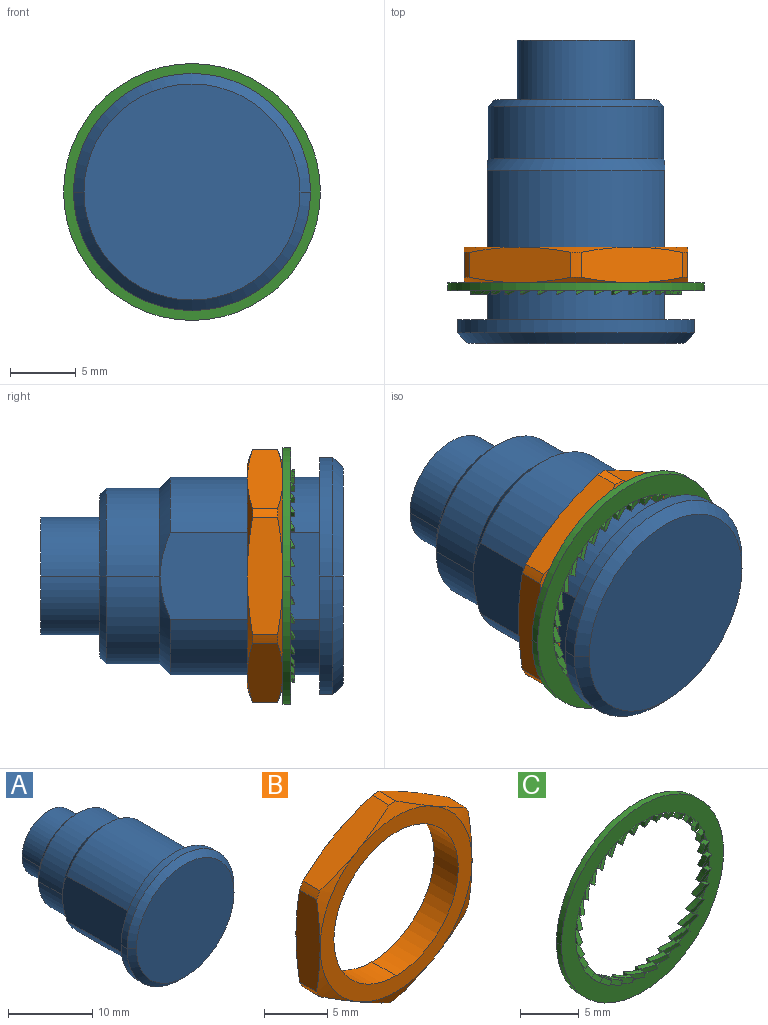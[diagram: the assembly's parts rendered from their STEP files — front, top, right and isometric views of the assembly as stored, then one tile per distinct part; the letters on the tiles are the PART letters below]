
ASSEMBLY  parts=3 mates=4
PART A: 20 faces, bbox 18x23x18 mm
  f0: cylinder r=4.45mm len=8.9mm, axis (0,-1,0), area 62.9mm2, adj f1,f2,f5
  f1: plane 8.9x8.9mm, normal (0,1,0), area 62.2mm2, adj f0,f2
  f2: cylinder r=4.45mm len=8.9mm, axis (0,-1,0), area 62.9mm2, adj f0,f1,f5
  f3: cylinder r=6.65mm len=13.3mm, axis (0,-1,0), area 83.6mm2, adj f4,f7,f18
  f4: cone r=6.15mm half-angle=45deg, axis (0,-1,0), area 14.2mm2, adj f3,f5,f6
  f5: plane 12.3x12.3mm, normal (0,1,0), area 56.6mm2, adj f0,f2,f4,f6
  f6: cone r=6.15mm half-angle=45deg, axis (0,-1,0), area 14.2mm2, adj f4,f5,f7
  f7: cylinder r=6.65mm len=13.3mm, axis (0,-1,0), area 83.6mm2, adj f3,f6,f17
  f8: plane 12.1x6.54mm, normal (1,0,0), area 77.4mm2, adj f9,f15,f16,f17,f18
  f9: cylinder r=7.5mm len=13.5mm, axis (0,-1,0), area 190.6mm2, adj f8,f15,f18,f19
  f10: plane 16.4x16.4mm, normal (0,-1,0), area 211.2mm2, adj f11,f12
  f11: cone r=8.2mm half-angle=45deg, axis (0,1,0), area 30.6mm2, adj f10,f12,f14
  f12: cone r=8.2mm half-angle=45deg, axis (0,1,0), area 30.6mm2, adj f10,f11,f13
  f13: cylinder r=9mm len=18mm, axis (0,-1,0), area 28.3mm2, adj f12,f14,f15
  f14: cylinder r=9mm len=18mm, axis (0,-1,0), area 28.3mm2, adj f11,f13,f15
  f15: plane 18x18mm, normal (0,1,0), area 84.4mm2, adj f8,f9,f13,f14,f16,f19
  f16: cylinder r=7.5mm len=13.5mm, axis (0,-1,0), area 190.6mm2, adj f8,f15,f17,f19
  f17: cone r=6.65mm half-angle=45deg, axis (0,-1,0), area 22mm2, adj f7,f8,f16,f18,f19
  f18: cone r=6.65mm half-angle=45deg, axis (0,-1,0), area 22mm2, adj f3,f8,f9,f17,f19
  f19: plane 12.1x6.54mm, normal (-1,0,0), area 77.4mm2, adj f9,f15,f16,f17,f18
PART B: 28 faces, bbox 19.2x2.7x19.2 mm
  f0: cone r=8.5mm half-angle=70deg, axis (0,1,0), area 4mm2, adj f1,f15,f17,f26
  f1: cylinder r=9.6mm len=1.9mm, axis (0,1,0), area 1.5mm2, adj f0,f15,f16,f17
  f2: cone r=8.5mm half-angle=70deg, axis (0,1,0), area 4mm2, adj f3,f13,f15,f26
  f3: cylinder r=9.6mm len=1.9mm, axis (0,1,0), area 1.5mm2, adj f2,f13,f14,f15
  f4: cylinder r=6.96mm len=13.92mm, axis (0,1,0), area 59mm2, adj f5,f26,f27
  f5: plane 17x17mm, normal (0,1,0), area 74.9mm2, adj f4,f8,f12,f14,f16,f20,f23,f27
  f6: cone r=8.5mm half-angle=70deg, axis (0,1,0), area 4mm2, adj f7,f9,f24,f26
  f7: cylinder r=9.6mm len=1.9mm, axis (0,1,0), area 1.5mm2, adj f6,f8,f9,f24
  f8: cone r=8.5mm half-angle=70deg, axis (0,-1,0), area 4mm2, adj f5,f7,f9,f24
  f9: plane 7.73x4.46mm, normal (0.5,0,-0.87), area 21.7mm2, adj f6,f7,f8,f10,f11,f12
  f10: cone r=8.5mm half-angle=70deg, axis (0,1,0), area 4mm2, adj f9,f11,f13,f26
  f11: cylinder r=9.6mm len=1.9mm, axis (0,1,0), area 1.5mm2, adj f9,f10,f12,f13
  f12: cone r=8.5mm half-angle=70deg, axis (0,-1,0), area 4mm2, adj f5,f9,f11,f13
  f13: plane 7.73x4.46mm, normal (-0.5,0,-0.87), area 21.7mm2, adj f2,f3,f10,f11,f12,f14
  f14: cone r=8.5mm half-angle=70deg, axis (0,-1,0), area 4mm2, adj f3,f5,f13,f15
  f15: plane 8.92x2.7mm, normal (-1,0,0), area 21.7mm2, adj f0,f1,f2,f3,f14,f16
  f16: cone r=8.5mm half-angle=70deg, axis (0,-1,0), area 4mm2, adj f1,f5,f15,f17
  f17: plane 7.73x4.46mm, normal (-0.5,0,0.87), area 21.7mm2, adj f0,f1,f16,f18,f19,f20
  f18: cone r=8.5mm half-angle=70deg, axis (0,1,0), area 4mm2, adj f17,f19,f21,f26
  f19: cylinder r=9.6mm len=1.9mm, axis (0,1,0), area 1.5mm2, adj f17,f18,f20,f21
  f20: cone r=8.5mm half-angle=70deg, axis (0,-1,0), area 4mm2, adj f5,f17,f19,f21
  f21: plane 7.73x4.46mm, normal (0.5,0,0.87), area 21.7mm2, adj f18,f19,f20,f22,f23,f25
  f22: cylinder r=9.6mm len=1.9mm, axis (0,1,0), area 1.5mm2, adj f21,f23,f24,f25
  f23: cone r=8.5mm half-angle=70deg, axis (0,-1,0), area 4mm2, adj f5,f21,f22,f24
  f24: plane 8.92x2.7mm, normal (1,0,0), area 21.7mm2, adj f6,f7,f8,f22,f23,f25
  f25: cone r=8.5mm half-angle=70deg, axis (0,1,0), area 4mm2, adj f21,f22,f24,f26
  f26: plane 17x17mm, normal (0,-1,0), area 74.9mm2, adj f0,f2,f4,f6,f10,f18,f25,f27
  f27: cylinder r=6.96mm len=13.92mm, axis (0,1,0), area 59mm2, adj f4,f5,f26
PART C: 276 faces, bbox 19.5x1.2x19.5 mm
  f0: cylinder r=8.05mm len=0.68mm, axis (0,1,0), area 0.1mm2, adj f269,f271,f272
  f1: cylinder r=8.05mm len=0.68mm, axis (0,1,0), area 0.1mm2, adj f266,f273,f274
  f2: bspline ~1.51x0.79mm, area 0.8mm2, adj f3,f4,f8,f9,f13
  f3: cylinder r=8.05mm len=0.67mm, axis (0,1,0), area 0.1mm2, adj f2,f4,f269
  f4: plane 0.55x0.5mm, normal (-0.1,0,-0.99), area 0.3mm2, adj f2,f3,f5,f7,f8
  f5: cylinder r=8.05mm len=1.6mm, axis (0,-1,0), area 0.3mm2, adj f4,f7,f266,f269,f272,f273
  f6: cylinder r=8.05mm len=0.66mm, axis (0,1,0), area 0.1mm2, adj f7,f9,f266
  f7: bspline ~1.51x0.79mm, area 0.8mm2, adj f4,f5,f6,f8,f9
  f8: cylinder r=7.55mm len=1.37mm, axis (0,1,0), area 0.8mm2, adj f2,f4,f7,f9
  f9: plane 0.55x0.48mm, normal (0.26,0,0.97), area 0.3mm2, adj f2,f6,f7,f8,f13
  f10: bspline ~1.53x1.02mm, area 0.8mm2, adj f11,f12,f16,f17,f21
  f11: cylinder r=8.05mm len=0.64mm, axis (0,1,0), area 0.1mm2, adj f10,f12,f269
  f12: plane 0.55x0.48mm, normal (-0.29,0,-0.96), area 0.3mm2, adj f10,f11,f13,f15,f16
  f13: cylinder r=8.05mm len=1.54mm, axis (0,-1,0), area 0.3mm2, adj f2,f9,f12,f15,f266,f269
  f14: cylinder r=8.05mm len=0.62mm, axis (0,1,0), area 0.1mm2, adj f15,f17,f266
  f15: bspline ~1.53x1.02mm, area 0.8mm2, adj f12,f13,f14,f16,f17
  f16: cylinder r=7.55mm len=1.3mm, axis (0,1,0), area 0.8mm2, adj f10,f12,f15,f17
  f17: plane 0.55x0.45mm, normal (0.43,0,0.9), area 0.3mm2, adj f10,f14,f15,f16,f21
  f18: bspline ~1.5x1.21mm, area 0.8mm2, adj f19,f20,f24,f25,f29
  f19: cylinder r=8.05mm len=0.59mm, axis (0,1,0), area 0.1mm2, adj f18,f20,f269
  f20: plane 0.55x0.44mm, normal (-0.46,0,-0.89), area 0.3mm2, adj f18,f19,f21,f23,f24
  f21: cylinder r=8.05mm len=1.44mm, axis (0,-1,0), area 0.3mm2, adj f10,f17,f20,f23,f266,f269
  f22: cylinder r=8.05mm len=0.56mm, axis (0,1,0), area 0.1mm2, adj f23,f25,f266
  f23: bspline ~1.5x1.21mm, area 0.8mm2, adj f20,f21,f22,f24,f25
  f24: cylinder r=7.55mm len=1.2mm, axis (0,1,0), area 0.8mm2, adj f18,f20,f23,f25
  f25: plane 0.55x0.4mm, normal (0.59,0,0.81), area 0.3mm2, adj f18,f22,f23,f24,f29
  f26: bspline ~1.42x1.36mm, area 0.8mm2, adj f27,f28,f32,f33,f37
  f27: cylinder r=8.05mm len=0.52mm, axis (0,1,0), area 0.1mm2, adj f26,f28,f269
  f28: plane 0.55x0.4mm, normal (-0.61,0,-0.79), area 0.3mm2, adj f26,f27,f29,f31,f32
  f29: cylinder r=8.05mm len=1.28mm, axis (0,-1,0), area 0.3mm2, adj f18,f25,f28,f31,f266,f269
  f30: cylinder r=8.05mm len=0.48mm, axis (0,1,0), area 0.1mm2, adj f31,f33,f266
  f31: bspline ~1.42x1.36mm, area 0.8mm2, adj f28,f29,f30,f32,f33
  f32: cylinder r=7.55mm len=1.2mm, axis (0,1,0), area 0.8mm2, adj f26,f28,f31,f33
  f33: plane 0.55x0.37mm, normal (0.73,0,0.68), area 0.3mm2, adj f26,f30,f31,f32,f37
  f34: bspline ~1.47x1.29mm, area 0.8mm2, adj f35,f36,f40,f41,f45
  f35: cylinder r=8.05mm len=0.52mm, axis (0,1,0), area 0.1mm2, adj f34,f36,f269
  f36: plane 0.55x0.37mm, normal (-0.75,0,-0.66), area 0.3mm2, adj f34,f35,f37,f39,f40
  f37: cylinder r=8.05mm len=1.19mm, axis (0,-1,0), area 0.3mm2, adj f26,f33,f36,f39,f266,f269
  f38: cylinder r=8.05mm len=0.56mm, axis (0,1,0), area 0.1mm2, adj f39,f41,f266
  f39: bspline ~1.47x1.29mm, area 0.8mm2, adj f36,f37,f38,f40,f41
  f40: cylinder r=7.55mm len=1.2mm, axis (0,1,0), area 0.8mm2, adj f34,f36,f39,f41
  f41: plane 0.55x0.42mm, normal (0.84,0,0.54), area 0.3mm2, adj f34,f38,f39,f40,f45
  f42: bspline ~1.53x1.12mm, area 0.8mm2, adj f43,f44,f48,f49,f53
  f43: cylinder r=8.05mm len=0.59mm, axis (0,1,0), area 0.1mm2, adj f42,f44,f269
  f44: plane 0.55x0.43mm, normal (-0.86,0,-0.52), area 0.3mm2, adj f42,f43,f45,f47,f48
  f45: cylinder r=8.05mm len=1.36mm, axis (0,-1,0), area 0.3mm2, adj f34,f41,f44,f47,f266,f269
  f46: cylinder r=8.05mm len=0.62mm, axis (0,1,0), area 0.1mm2, adj f47,f49,f266
  f47: bspline ~1.53x1.12mm, area 0.8mm2, adj f44,f45,f46,f48,f49
  f48: cylinder r=7.55mm len=1.25mm, axis (0,1,0), area 0.8mm2, adj f42,f44,f47,f49
  f49: plane 0.55x0.46mm, normal (0.93,0,0.37), area 0.3mm2, adj f42,f46,f47,f48,f53
  f50: bspline ~1.53x0.91mm, area 0.8mm2, adj f51,f52,f56,f57,f61
  f51: cylinder r=8.05mm len=0.64mm, axis (0,1,0), area 0.1mm2, adj f50,f52,f269
  f52: plane 0.55x0.47mm, normal (-0.94,0,-0.35), area 0.3mm2, adj f50,f51,f53,f55,f56
  f53: cylinder r=8.05mm len=1.5mm, axis (0,-1,0), area 0.3mm2, adj f42,f49,f52,f55,f266,f269
  f54: cylinder r=8.05mm len=0.66mm, axis (0,1,0), area 0.1mm2, adj f55,f57,f266
  f55: bspline ~1.53x0.91mm, area 0.8mm2, adj f52,f53,f54,f56,f57
  f56: cylinder r=7.55mm len=1.34mm, axis (0,1,0), area 0.8mm2, adj f50,f52,f55,f57
  f57: plane 0.55x0.49mm, normal (0.98,0,0.2), area 0.3mm2, adj f50,f54,f55,f56,f61
  f58: bspline ~1.48x0.67mm, area 0.8mm2, adj f59,f60,f64,f65,f69
  f59: cylinder r=8.05mm len=0.67mm, axis (0,1,0), area 0.1mm2, adj f58,f60,f269
  f60: plane 0.55x0.49mm, normal (-0.99,0,-0.17), area 0.3mm2, adj f58,f59,f61,f63,f64
  f61: cylinder r=8.05mm len=1.58mm, axis (0,-1,0), area 0.3mm2, adj f50,f57,f60,f63,f266,f269
  f62: cylinder r=8.05mm len=0.68mm, axis (0,1,0), area 0.1mm2, adj f63,f65,f266
  f63: bspline ~1.48x0.67mm, area 0.8mm2, adj f60,f61,f62,f64,f65
  f64: cylinder r=7.55mm len=1.39mm, axis (0,1,0), area 0.8mm2, adj f58,f60,f63,f65
  f65: plane 0.55x0.5mm, normal (1,0,0.01), area 0.3mm2, adj f58,f62,f63,f64,f69
  f66: bspline ~1.48x0.67mm, area 0.8mm2, adj f67,f68,f72,f73,f77
  f67: cylinder r=8.05mm len=0.68mm, axis (0,1,0), area 0.1mm2, adj f66,f68,f269
  f68: plane 0.55x0.5mm, normal (-1,0,0.01), area 0.3mm2, adj f66,f67,f69,f71,f72
  f69: cylinder r=8.05mm len=1.6mm, axis (0,-1,0), area 0.3mm2, adj f58,f65,f68,f71,f266,f269
  f70: cylinder r=8.05mm len=0.67mm, axis (0,1,0), area 0.1mm2, adj f71,f73,f266
  f71: bspline ~1.48x0.67mm, area 0.8mm2, adj f68,f69,f70,f72,f73
  f72: cylinder r=7.55mm len=1.39mm, axis (0,1,0), area 0.8mm2, adj f66,f68,f71,f73
  f73: plane 0.55x0.49mm, normal (0.99,0,-0.17), area 0.3mm2, adj f66,f70,f71,f72,f77
  f74: bspline ~1.53x0.91mm, area 0.8mm2, adj f75,f76,f80,f81,f85
  f75: cylinder r=8.05mm len=0.66mm, axis (0,1,0), area 0.1mm2, adj f74,f76,f269
  f76: plane 0.55x0.49mm, normal (-0.98,0,0.2), area 0.3mm2, adj f74,f75,f77,f79,f80
  f77: cylinder r=8.05mm len=1.58mm, axis (0,-1,0), area 0.3mm2, adj f66,f73,f76,f79,f266,f269
  f78: cylinder r=8.05mm len=0.64mm, axis (0,1,0), area 0.1mm2, adj f79,f81,f266
  f79: bspline ~1.53x0.91mm, area 0.8mm2, adj f76,f77,f78,f80,f81
  f80: cylinder r=7.55mm len=1.34mm, axis (0,1,0), area 0.8mm2, adj f74,f76,f79,f81
  f81: plane 0.55x0.47mm, normal (0.94,0,-0.35), area 0.3mm2, adj f74,f78,f79,f80,f85
  f82: bspline ~1.53x1.12mm, area 0.8mm2, adj f83,f84,f88,f89,f93
  f83: cylinder r=8.05mm len=0.62mm, axis (0,1,0), area 0.1mm2, adj f82,f84,f269
  f84: plane 0.55x0.46mm, normal (-0.93,0,0.37), area 0.3mm2, adj f82,f83,f85,f87,f88
  f85: cylinder r=8.05mm len=1.5mm, axis (0,-1,0), area 0.3mm2, adj f74,f81,f84,f87,f266,f269
  f86: cylinder r=8.05mm len=0.59mm, axis (0,1,0), area 0.1mm2, adj f87,f89,f266
  f87: bspline ~1.53x1.12mm, area 0.8mm2, adj f84,f85,f86,f88,f89
  f88: cylinder r=7.55mm len=1.25mm, axis (0,1,0), area 0.8mm2, adj f82,f84,f87,f89
  f89: plane 0.55x0.43mm, normal (0.86,0,-0.52), area 0.3mm2, adj f82,f86,f87,f88,f93
  f90: bspline ~1.47x1.29mm, area 0.8mm2, adj f91,f92,f96,f97,f101
  f91: cylinder r=8.05mm len=0.56mm, axis (0,1,0), area 0.1mm2, adj f90,f92,f269
  f92: plane 0.55x0.42mm, normal (-0.84,0,0.54), area 0.3mm2, adj f90,f91,f93,f95,f96
  f93: cylinder r=8.05mm len=1.36mm, axis (0,-1,0), area 0.3mm2, adj f82,f89,f92,f95,f266,f269
  f94: cylinder r=8.05mm len=0.52mm, axis (0,1,0), area 0.1mm2, adj f95,f97,f266
  f95: bspline ~1.47x1.29mm, area 0.8mm2, adj f92,f93,f94,f96,f97
  f96: cylinder r=7.55mm len=1.2mm, axis (0,1,0), area 0.8mm2, adj f90,f92,f95,f97
  f97: plane 0.55x0.37mm, normal (0.75,0,-0.66), area 0.3mm2, adj f90,f94,f95,f96,f101
  f98: bspline ~1.42x1.36mm, area 0.8mm2, adj f99,f100,f104,f105,f109
  f99: cylinder r=8.05mm len=0.48mm, axis (0,1,0), area 0.1mm2, adj f98,f100,f269
  f100: plane 0.55x0.37mm, normal (-0.73,0,0.68), area 0.3mm2, adj f98,f99,f101,f103,f104
  f101: cylinder r=8.05mm len=1.19mm, axis (0,-1,0), area 0.3mm2, adj f90,f97,f100,f103,f266,f269
  f102: cylinder r=8.05mm len=0.52mm, axis (0,1,0), area 0.1mm2, adj f103,f105,f266
  f103: bspline ~1.42x1.36mm, area 0.8mm2, adj f100,f101,f102,f104,f105
  f104: cylinder r=7.55mm len=1.2mm, axis (0,1,0), area 0.8mm2, adj f98,f100,f103,f105
  f105: plane 0.55x0.4mm, normal (0.61,0,-0.79), area 0.3mm2, adj f98,f102,f103,f104,f109
  f106: bspline ~1.5x1.21mm, area 0.8mm2, adj f107,f108,f112,f113,f117
  f107: cylinder r=8.05mm len=0.56mm, axis (0,1,0), area 0.1mm2, adj f106,f108,f269
  f108: plane 0.55x0.4mm, normal (-0.59,0,0.81), area 0.3mm2, adj f106,f107,f109,f111,f112
  f109: cylinder r=8.05mm len=1.28mm, axis (0,-1,0), area 0.3mm2, adj f98,f105,f108,f111,f266,f269
  f110: cylinder r=8.05mm len=0.59mm, axis (0,1,0), area 0.1mm2, adj f111,f113,f266
  f111: bspline ~1.5x1.21mm, area 0.8mm2, adj f108,f109,f110,f112,f113
  f112: cylinder r=7.55mm len=1.2mm, axis (0,1,0), area 0.8mm2, adj f106,f108,f111,f113
  f113: plane 0.55x0.44mm, normal (0.46,0,-0.89), area 0.3mm2, adj f106,f110,f111,f112,f117
  f114: bspline ~1.53x1.02mm, area 0.8mm2, adj f115,f116,f120,f121,f125
  f115: cylinder r=8.05mm len=0.62mm, axis (0,1,0), area 0.1mm2, adj f114,f116,f269
  f116: plane 0.55x0.45mm, normal (-0.43,0,0.9), area 0.3mm2, adj f114,f115,f117,f119,f120
  f117: cylinder r=8.05mm len=1.44mm, axis (0,-1,0), area 0.3mm2, adj f106,f113,f116,f119,f266,f269
  f118: cylinder r=8.05mm len=0.64mm, axis (0,1,0), area 0.1mm2, adj f119,f121,f266
  f119: bspline ~1.53x1.02mm, area 0.8mm2, adj f116,f117,f118,f120,f121
  f120: cylinder r=7.55mm len=1.3mm, axis (0,1,0), area 0.8mm2, adj f114,f116,f119,f121
  f121: plane 0.55x0.48mm, normal (0.29,0,-0.96), area 0.3mm2, adj f114,f118,f119,f120,f125
  f122: bspline ~1.51x0.79mm, area 0.8mm2, adj f123,f124,f128,f129,f133
  f123: cylinder r=8.05mm len=0.66mm, axis (0,1,0), area 0.1mm2, adj f122,f124,f269
  f124: plane 0.55x0.48mm, normal (-0.26,0,0.97), area 0.3mm2, adj f122,f123,f125,f127,f128
  f125: cylinder r=8.05mm len=1.54mm, axis (0,-1,0), area 0.3mm2, adj f114,f121,f124,f127,f266,f269
  f126: cylinder r=8.05mm len=0.67mm, axis (0,1,0), area 0.1mm2, adj f127,f129,f266
  f127: bspline ~1.51x0.79mm, area 0.8mm2, adj f124,f125,f126,f128,f129
  f128: cylinder r=7.55mm len=1.37mm, axis (0,1,0), area 0.8mm2, adj f122,f124,f127,f129
  f129: plane 0.55x0.5mm, normal (0.1,0,-0.99), area 0.3mm2, adj f122,f126,f127,f128,f133
  f130: bspline ~1.48x0.65mm, area 0.8mm2, adj f131,f132,f136,f137,f141
  f131: cylinder r=8.05mm len=0.68mm, axis (0,1,0), area 0.1mm2, adj f130,f132,f269
  f132: plane 0.55x0.5mm, normal (-0.08,0,1), area 0.3mm2, adj f130,f131,f133,f135,f136
  f133: cylinder r=8.05mm len=1.6mm, axis (0,-1,0), area 0.3mm2, adj f122,f129,f132,f135,f266,f269
  f134: cylinder r=8.05mm len=0.68mm, axis (0,1,0), area 0.1mm2, adj f135,f137,f266
  f135: bspline ~1.48x0.65mm, area 0.8mm2, adj f132,f133,f134,f136,f137
  f136: cylinder r=7.55mm len=1.39mm, axis (0,1,0), area 0.8mm2, adj f130,f132,f135,f137
  f137: plane 0.55x0.5mm, normal (-0.08,0,-1), area 0.3mm2, adj f130,f134,f135,f136,f141
  f138: bspline ~1.51x0.79mm, area 0.8mm2, adj f139,f140,f144,f145,f149
  f139: cylinder r=8.05mm len=0.67mm, axis (0,1,0), area 0.1mm2, adj f138,f140,f269
  f140: plane 0.55x0.5mm, normal (0.1,0,0.99), area 0.3mm2, adj f138,f139,f141,f143,f144
  f141: cylinder r=8.05mm len=1.6mm, axis (0,-1,0), area 0.3mm2, adj f130,f137,f140,f143,f266,f269
  f142: cylinder r=8.05mm len=0.66mm, axis (0,1,0), area 0.1mm2, adj f143,f145,f266
  f143: bspline ~1.51x0.79mm, area 0.8mm2, adj f140,f141,f142,f144,f145
  f144: cylinder r=7.55mm len=1.37mm, axis (0,1,0), area 0.8mm2, adj f138,f140,f143,f145
  f145: plane 0.55x0.48mm, normal (-0.26,0,-0.97), area 0.3mm2, adj f138,f142,f143,f144,f149
  f146: bspline ~1.53x1.02mm, area 0.8mm2, adj f147,f148,f152,f153,f157
  f147: cylinder r=8.05mm len=0.64mm, axis (0,1,0), area 0.1mm2, adj f146,f148,f269
  f148: plane 0.55x0.48mm, normal (0.29,0,0.96), area 0.3mm2, adj f146,f147,f149,f151,f152
  f149: cylinder r=8.05mm len=1.54mm, axis (0,-1,0), area 0.3mm2, adj f138,f145,f148,f151,f266,f269
  f150: cylinder r=8.05mm len=0.62mm, axis (0,1,0), area 0.1mm2, adj f151,f153,f266
  f151: bspline ~1.53x1.02mm, area 0.8mm2, adj f148,f149,f150,f152,f153
  f152: cylinder r=7.55mm len=1.3mm, axis (0,1,0), area 0.8mm2, adj f146,f148,f151,f153
  f153: plane 0.55x0.45mm, normal (-0.43,0,-0.9), area 0.3mm2, adj f146,f150,f151,f152,f157
  f154: bspline ~1.5x1.21mm, area 0.8mm2, adj f155,f156,f160,f161,f165
  f155: cylinder r=8.05mm len=0.59mm, axis (0,1,0), area 0.1mm2, adj f154,f156,f269
  f156: plane 0.55x0.44mm, normal (0.46,0,0.89), area 0.3mm2, adj f154,f155,f157,f159,f160
  f157: cylinder r=8.05mm len=1.44mm, axis (0,-1,0), area 0.3mm2, adj f146,f153,f156,f159,f266,f269
  f158: cylinder r=8.05mm len=0.56mm, axis (0,1,0), area 0.1mm2, adj f159,f161,f266
  f159: bspline ~1.5x1.21mm, area 0.8mm2, adj f156,f157,f158,f160,f161
  f160: cylinder r=7.55mm len=1.2mm, axis (0,1,0), area 0.8mm2, adj f154,f156,f159,f161
  f161: plane 0.55x0.4mm, normal (-0.59,0,-0.81), area 0.3mm2, adj f154,f158,f159,f160,f165
  f162: bspline ~1.42x1.36mm, area 0.8mm2, adj f163,f164,f168,f169,f173
  f163: cylinder r=8.05mm len=0.52mm, axis (0,1,0), area 0.1mm2, adj f162,f164,f269
  f164: plane 0.55x0.4mm, normal (0.61,0,0.79), area 0.3mm2, adj f162,f163,f165,f167,f168
  f165: cylinder r=8.05mm len=1.28mm, axis (0,-1,0), area 0.3mm2, adj f154,f161,f164,f167,f266,f269
  f166: cylinder r=8.05mm len=0.48mm, axis (0,1,0), area 0.1mm2, adj f167,f169,f266
  f167: bspline ~1.42x1.36mm, area 0.8mm2, adj f164,f165,f166,f168,f169
  f168: cylinder r=7.55mm len=1.2mm, axis (0,1,0), area 0.8mm2, adj f162,f164,f167,f169
  f169: plane 0.55x0.37mm, normal (-0.73,0,-0.68), area 0.3mm2, adj f162,f166,f167,f168,f173
  f170: bspline ~1.47x1.29mm, area 0.8mm2, adj f171,f172,f176,f177,f181
  f171: cylinder r=8.05mm len=0.52mm, axis (0,1,0), area 0.1mm2, adj f170,f172,f269
  f172: plane 0.55x0.37mm, normal (0.75,0,0.66), area 0.3mm2, adj f170,f171,f173,f175,f176
  f173: cylinder r=8.05mm len=1.19mm, axis (0,-1,0), area 0.3mm2, adj f162,f169,f172,f175,f266,f269
  f174: cylinder r=8.05mm len=0.56mm, axis (0,1,0), area 0.1mm2, adj f175,f177,f266
  f175: bspline ~1.47x1.29mm, area 0.8mm2, adj f172,f173,f174,f176,f177
  f176: cylinder r=7.55mm len=1.2mm, axis (0,1,0), area 0.8mm2, adj f170,f172,f175,f177
  f177: plane 0.55x0.42mm, normal (-0.84,0,-0.54), area 0.3mm2, adj f170,f174,f175,f176,f181
  f178: bspline ~1.53x1.12mm, area 0.8mm2, adj f179,f180,f184,f185,f189
  f179: cylinder r=8.05mm len=0.59mm, axis (0,1,0), area 0.1mm2, adj f178,f180,f269
  f180: plane 0.55x0.43mm, normal (0.86,0,0.52), area 0.3mm2, adj f178,f179,f181,f183,f184
  f181: cylinder r=8.05mm len=1.36mm, axis (0,-1,0), area 0.3mm2, adj f170,f177,f180,f183,f266,f269
  f182: cylinder r=8.05mm len=0.62mm, axis (0,1,0), area 0.1mm2, adj f183,f185,f266
  f183: bspline ~1.53x1.12mm, area 0.8mm2, adj f180,f181,f182,f184,f185
  f184: cylinder r=7.55mm len=1.25mm, axis (0,1,0), area 0.8mm2, adj f178,f180,f183,f185
  f185: plane 0.55x0.46mm, normal (-0.93,0,-0.37), area 0.3mm2, adj f178,f182,f183,f184,f189
  f186: bspline ~1.53x0.91mm, area 0.8mm2, adj f187,f188,f192,f193,f197
  f187: cylinder r=8.05mm len=0.64mm, axis (0,1,0), area 0.1mm2, adj f186,f188,f269
  f188: plane 0.55x0.47mm, normal (0.94,0,0.35), area 0.3mm2, adj f186,f187,f189,f191,f192
  f189: cylinder r=8.05mm len=1.5mm, axis (0,-1,0), area 0.3mm2, adj f178,f185,f188,f191,f266,f269
  f190: cylinder r=8.05mm len=0.66mm, axis (0,1,0), area 0.1mm2, adj f191,f193,f266
  f191: bspline ~1.53x0.91mm, area 0.8mm2, adj f188,f189,f190,f192,f193
  f192: cylinder r=7.55mm len=1.34mm, axis (0,1,0), area 0.8mm2, adj f186,f188,f191,f193
  f193: plane 0.55x0.49mm, normal (-0.98,0,-0.2), area 0.3mm2, adj f186,f190,f191,f192,f197
  f194: bspline ~1.48x0.67mm, area 0.8mm2, adj f195,f196,f200,f201,f265
  f195: cylinder r=8.05mm len=0.67mm, axis (0,1,0), area 0.1mm2, adj f194,f196,f269
  f196: plane 0.55x0.49mm, normal (0.99,0,0.17), area 0.3mm2, adj f194,f195,f197,f199,f200
  f197: cylinder r=8.05mm len=1.58mm, axis (0,-1,0), area 0.3mm2, adj f186,f193,f196,f199,f266,f269
  f198: cylinder r=8.05mm len=0.68mm, axis (0,1,0), area 0.1mm2, adj f199,f201,f266
  f199: bspline ~1.48x0.67mm, area 0.8mm2, adj f196,f197,f198,f200,f201
  f200: cylinder r=7.55mm len=1.39mm, axis (0,1,0), area 0.8mm2, adj f194,f196,f199,f201
  f201: plane 0.55x0.5mm, normal (-1,0,-0.01), area 0.3mm2, adj f194,f198,f199,f200,f265
  f202: cylinder r=8.05mm len=0.67mm, axis (0,1,0), area 0.1mm2, adj f261,f262,f266
  f203: cylinder r=8.05mm len=0.64mm, axis (0,1,0), area 0.1mm2, adj f254,f255,f266
  f204: cylinder r=8.05mm len=0.59mm, axis (0,1,0), area 0.1mm2, adj f247,f248,f266
  f205: cylinder r=8.05mm len=0.52mm, axis (0,1,0), area 0.1mm2, adj f240,f241,f266
  f206: cylinder r=8.05mm len=0.52mm, axis (0,1,0), area 0.1mm2, adj f233,f234,f266
  f207: cylinder r=8.05mm len=0.59mm, axis (0,1,0), area 0.1mm2, adj f226,f227,f266
  f208: cylinder r=8.05mm len=0.64mm, axis (0,1,0), area 0.1mm2, adj f219,f220,f266
  f209: cylinder r=8.05mm len=0.67mm, axis (0,1,0), area 0.1mm2, adj f212,f213,f266
  f210: cylinder r=8.05mm len=0.66mm, axis (0,1,0), area 0.1mm2, adj f211,f215,f269
  f211: bspline ~1.51x0.79mm, area 0.8mm2, adj f210,f212,f214,f215,f270
  f212: plane 0.55x0.5mm, normal (-0.1,0,0.99), area 0.3mm2, adj f209,f211,f213,f214,f270
  f213: bspline ~1.51x0.79mm, area 0.8mm2, adj f209,f212,f214,f215,f216
  f214: cylinder r=7.55mm len=1.37mm, axis (0,1,0), area 0.8mm2, adj f211,f212,f213,f215
  f215: plane 0.55x0.48mm, normal (0.26,0,-0.97), area 0.3mm2, adj f210,f211,f213,f214,f216
  f216: cylinder r=8.05mm len=1.54mm, axis (0,-1,0), area 0.3mm2, adj f213,f215,f218,f219,f266,f269
  f217: cylinder r=8.05mm len=0.62mm, axis (0,1,0), area 0.1mm2, adj f218,f222,f269
  f218: bspline ~1.53x1.02mm, area 0.8mm2, adj f216,f217,f219,f221,f222
  f219: plane 0.55x0.48mm, normal (-0.29,0,0.96), area 0.3mm2, adj f208,f216,f218,f220,f221
  f220: bspline ~1.53x1.02mm, area 0.8mm2, adj f208,f219,f221,f222,f223
  f221: cylinder r=7.55mm len=1.3mm, axis (0,1,0), area 0.8mm2, adj f218,f219,f220,f222
  f222: plane 0.55x0.45mm, normal (0.43,0,-0.9), area 0.3mm2, adj f217,f218,f220,f221,f223
  f223: cylinder r=8.05mm len=1.44mm, axis (0,-1,0), area 0.3mm2, adj f220,f222,f225,f226,f266,f269
  f224: cylinder r=8.05mm len=0.56mm, axis (0,1,0), area 0.1mm2, adj f225,f229,f269
  f225: bspline ~1.5x1.21mm, area 0.8mm2, adj f223,f224,f226,f228,f229
  f226: plane 0.55x0.44mm, normal (-0.46,0,0.89), area 0.3mm2, adj f207,f223,f225,f227,f228
  f227: bspline ~1.5x1.21mm, area 0.8mm2, adj f207,f226,f228,f229,f230
  f228: cylinder r=7.55mm len=1.2mm, axis (0,1,0), area 0.8mm2, adj f225,f226,f227,f229
  f229: plane 0.55x0.4mm, normal (0.59,0,-0.81), area 0.3mm2, adj f224,f225,f227,f228,f230
  f230: cylinder r=8.05mm len=1.28mm, axis (0,-1,0), area 0.3mm2, adj f227,f229,f232,f233,f266,f269
  f231: cylinder r=8.05mm len=0.48mm, axis (0,1,0), area 0.1mm2, adj f232,f236,f269
  f232: bspline ~1.42x1.36mm, area 0.8mm2, adj f230,f231,f233,f235,f236
  f233: plane 0.55x0.4mm, normal (-0.61,0,0.79), area 0.3mm2, adj f206,f230,f232,f234,f235
  f234: bspline ~1.42x1.36mm, area 0.8mm2, adj f206,f233,f235,f236,f237
  f235: cylinder r=7.55mm len=1.2mm, axis (0,1,0), area 0.8mm2, adj f232,f233,f234,f236
  f236: plane 0.55x0.37mm, normal (0.73,0,-0.68), area 0.3mm2, adj f231,f232,f234,f235,f237
  f237: cylinder r=8.05mm len=1.19mm, axis (0,-1,0), area 0.3mm2, adj f234,f236,f239,f240,f266,f269
  f238: cylinder r=8.05mm len=0.56mm, axis (0,1,0), area 0.1mm2, adj f239,f243,f269
  f239: bspline ~1.47x1.29mm, area 0.8mm2, adj f237,f238,f240,f242,f243
  f240: plane 0.55x0.37mm, normal (-0.75,0,0.66), area 0.3mm2, adj f205,f237,f239,f241,f242
  f241: bspline ~1.47x1.29mm, area 0.8mm2, adj f205,f240,f242,f243,f244
  f242: cylinder r=7.55mm len=1.2mm, axis (0,1,0), area 0.8mm2, adj f239,f240,f241,f243
  f243: plane 0.55x0.42mm, normal (0.84,0,-0.54), area 0.3mm2, adj f238,f239,f241,f242,f244
  f244: cylinder r=8.05mm len=1.36mm, axis (0,-1,0), area 0.3mm2, adj f241,f243,f246,f247,f266,f269
  f245: cylinder r=8.05mm len=0.62mm, axis (0,1,0), area 0.1mm2, adj f246,f250,f269
  f246: bspline ~1.53x1.12mm, area 0.8mm2, adj f244,f245,f247,f249,f250
  f247: plane 0.55x0.43mm, normal (-0.86,0,0.52), area 0.3mm2, adj f204,f244,f246,f248,f249
  f248: bspline ~1.53x1.12mm, area 0.8mm2, adj f204,f247,f249,f250,f251
  f249: cylinder r=7.55mm len=1.25mm, axis (0,1,0), area 0.8mm2, adj f246,f247,f248,f250
  f250: plane 0.55x0.46mm, normal (0.93,0,-0.37), area 0.3mm2, adj f245,f246,f248,f249,f251
  f251: cylinder r=8.05mm len=1.5mm, axis (0,-1,0), area 0.3mm2, adj f248,f250,f253,f254,f266,f269
  f252: cylinder r=8.05mm len=0.66mm, axis (0,1,0), area 0.1mm2, adj f253,f257,f269
  f253: bspline ~1.53x0.91mm, area 0.8mm2, adj f251,f252,f254,f256,f257
  f254: plane 0.55x0.47mm, normal (-0.94,0,0.35), area 0.3mm2, adj f203,f251,f253,f255,f256
  f255: bspline ~1.53x0.91mm, area 0.8mm2, adj f203,f254,f256,f257,f258
  f256: cylinder r=7.55mm len=1.34mm, axis (0,1,0), area 0.8mm2, adj f253,f254,f255,f257
  f257: plane 0.55x0.49mm, normal (0.98,0,-0.2), area 0.3mm2, adj f252,f253,f255,f256,f258
  f258: cylinder r=8.05mm len=1.58mm, axis (0,-1,0), area 0.3mm2, adj f255,f257,f260,f261,f266,f269
  f259: cylinder r=8.05mm len=0.68mm, axis (0,1,0), area 0.1mm2, adj f260,f264,f269
  f260: bspline ~1.48x0.67mm, area 0.8mm2, adj f258,f259,f261,f263,f264
  f261: plane 0.55x0.49mm, normal (-0.99,0,0.17), area 0.3mm2, adj f202,f258,f260,f262,f263
  f262: bspline ~1.48x0.67mm, area 0.8mm2, adj f202,f261,f263,f264,f265
  f263: cylinder r=7.55mm len=1.39mm, axis (0,1,0), area 0.8mm2, adj f260,f261,f262,f264
  f264: plane 0.55x0.5mm, normal (1,0,-0.01), area 0.3mm2, adj f259,f260,f262,f263,f265
  f265: cylinder r=8.05mm len=1.6mm, axis (0,-1,0), area 0.3mm2, adj f194,f201,f262,f264,f266,f269
  f266: plane 19.5x19.5mm, normal (0,1,0), area 95.1mm2, adj f1,f5,f6,f13,f14,f21,f22,f29
  f267: cylinder r=9.75mm len=19.5mm, axis (0,1,0), area 18.4mm2, adj f266,f268,f269
  f268: cylinder r=9.75mm len=19.5mm, axis (0,1,0), area 18.4mm2, adj f266,f267,f269
  f269: plane 19.5x19.5mm, normal (0,-1,0), area 95.1mm2, adj f0,f3,f5,f11,f13,f19,f21,f27
  f270: cylinder r=8.05mm len=1.6mm, axis (0,-1,0), area 0.3mm2, adj f211,f212,f266,f269,f271,f274
  f271: plane 0.55x0.5mm, normal (0.08,0,-1), area 0.3mm2, adj f0,f270,f272,f274,f275
  f272: bspline ~1.48x0.65mm, area 0.8mm2, adj f0,f5,f271,f273,f275
  f273: plane 0.55x0.5mm, normal (0.08,0,1), area 0.3mm2, adj f1,f5,f272,f274,f275
  f274: bspline ~1.48x0.65mm, area 0.8mm2, adj f1,f270,f271,f273,f275
  f275: cylinder r=7.55mm len=1.39mm, axis (0,1,0), area 0.8mm2, adj f271,f272,f273,f274
PLACE A t=(0,14.44,0)mm
PLACE B t=(0,7.82,0)mm
PLACE C t=(0,8.14,0)mm
MATE cylindrical C.f0 <-> A.f0  axis (0,1,0) through (0,18.74,0)mm
MATE cylindrical B.f0 <-> A.f0  axis (0,1,0) through (0,20.39,0)mm
MATE planar B.f0 <-> C.f0  axis (0,-1,0) through (0,19.04,0)mm
MATE planar C.f269 <-> A.f0  axis (0,-1,0) through (-8.02,18.44,0.75)mm
